# Revit family: Заслонка воздушная круглая Z с приводом
name_source: partatom
category: Арматура воздуховодов
units: mm (PartAtom-declared; Revit-internal decimal feet)

## family parameters
Всегда вертикально = Да
На основе рабочей плоскости = Нет
Общий = Нет
При загрузке вырезать с полостями = Нет
Размер круглого соединителя = Использовать диаметр
Тип детали = Вставляется

## types (6) — shared parameters
ADSK_Единица измерения = шт.
ADSK_Завод-изготовитель = Naveka
ADSK_Наименование = Заслонка воздушная
ADSK_Примечание = https://progress-nw.ru
Материал = RAL 0000 Серый металл
zero-valued in all types: ADSK_Масса

## per-type parameters (varying)
| type | ADSK_Марка | D | d | d+5 | d1 | h1 |
| Заслонка воздушная Z-250 | Z-250 | 250 мм | 243 мм | 248 мм | 124 мм | 142 мм |
| Заслонка воздушная Z-100 | Z-100 | 100 мм | 93 мм | 98 мм | 49 мм | 67 мм |
| Заслонка воздушная Z-125 | Z-125 | 125 мм | 118 мм | 123 мм | 62 мм | 80 мм |
| Заслонка воздушная Z-160 | Z-160 | 160 мм | 153 мм | 158 мм | 79 мм | 97 мм |
| Заслонка воздушная Z-200 | Z-200 | 200 мм | 193 мм | 198 мм | 99 мм | 117 мм |
| Заслонка воздушная Z-315 | Z-315 | 315 мм | 308 мм | 313 мм | 157 мм | 175 мм |
